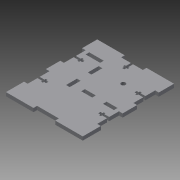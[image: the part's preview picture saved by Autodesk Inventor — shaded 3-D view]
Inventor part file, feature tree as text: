
AUTODESK INVENTOR PART (.ipt)
format: ipt  version: 2014 (Build 180170000, 170)  size: 206,848 bytes
history: native  units: mm
features: extrude x2, sketch x2, reference x1
ambient origin geometry x8: Origin, YZ Plane, XZ Plane, XY Plane, X Axis, Y Axis, Z Axis, Center Point
bodies: 实体1 (feature_tree)
feature tree (5):
  extrude  "拉伸1"  Depth=12.0mm
  extrude  "拉伸2"  [1 undecoded]
  sketch  "草图1"  dims[d0=5.0mm d1=0.0mm d2=12.0mm]
  reference  "参考1"
  sketch  "草图2"  dims[d3=5.0mm d4=0.0mm]
note: 1 required parameter value undecoded (feature->parameter linkage not recoverable at this tier; creation-order binding heuristic only, values carry confidence <= 0.55)
